# Revit family: FLAT LB_S LED
name_source: partatom
category: Осветительные приборы
revit_build: Autodesk Revit 2016 (Build: 20161004_0715(x64)
units: mm (PartAtom-declared; Revit-internal decimal feet)

## family parameters
Источник света = Нет
Общий = Нет
Основа = Грань
При загрузке вырезать с полостями = Нет
Размер круглого соединителя = Использовать диаметр
Тип детали = Нормальный
Точка расчета площади = Нет

## types (1)
- FLAT LB_S LED
    ADSK_Единица измерения = Шт.
    ADSK_Завод-изготовитель = ООО МГК Световые технологии
    ADSK_Классификация нагрузок = Прочее
    ADSK_Код изделия = 1334000780
    ADSK_Количество фаз = 1
    ADSK_Количество фаз числовое = 1
    ADSK_Коэффициент мощности = 0.96
    ADSK_Масса = 10
    ADSK_Наименование = Взрывозащищенный светодиодный светильник серии FLAT LED предназначен для освещения взрывоопасных зон всех классов помещений и наружных установок предприятий нефтегазовой и нефтехимической отрасли согласно маркировке взрывозащиты. Светильники характеризуются компактными габаритными размерами, высокой степенью IP и высокой энергоэффективностью
    ADSK_Напряжение = 230 В
    ADSK_Номинальная мощность = 0 кВт
    ADSK_Полная мощность = 0 кВ·А
    ADSK_Размер_Высота = 128 мм
    ADSK_Размер_Ширина = 335 мм
    ADSK_Ток = 0 А
    ADSK_Энергоэффективность = 100 лм/Вт
    IP Class = IP66
    URL = https://ltcompany.com
    Блок аварийного питания = Нет
    Выбор ИС = IES_FLAT LB_S LED : FLAT LB/S LED 100 D120 Ex 5000K
    Группа модели = Светильники
    Да = Нет
    Изготовитель = ООО МГК Световые технологии
    Излучатель = Плафон самосвечение
    Класс Защиты = I
    Класс пожароопасности = П-I,II,IIa,ІІІ
    Климатическая зона = УХЛ1
    Код по классификатору = D5020200
    Корпус = Белый металл
    Лира.высота = 190 мм
    Нет = Нет
    Область использования = Нефтегазовая промышленность
    Описание = Взрывозащищенный светодиодный светильник серии FLAT LED предназначен для освещения взрывоопасных зон всех классов помещений и наружных установок предприятий нефтегазовой и нефтехимической отрасли согласно маркировке взрывозащиты. Светильники характеризуются компактными габаритными размерами, высокой степенью IP и высокой энергоэффективностью
    Отметка по умолчанию = 0 мм
    Плафон = Плафон самосвечение
    Полная установленная мощность = 0 кВ·А
    Решетка = Cерый металл матовый
    Тип ИС = LED
    Тип ПРА = Драйвер
    Тип продукции = Светильник
